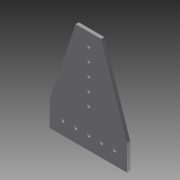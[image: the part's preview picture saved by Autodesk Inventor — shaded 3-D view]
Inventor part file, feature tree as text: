
AUTODESK INVENTOR PART (.ipt)
format: ipt  version: 2012 (Build 160160000, 160)  size: 92,160 bytes
history: native  units: in
note: dims shown in document units (in); Inventor stores cm internally (conversion verified against a paired STEP export)
features: extrude x1, sketch x1
ambient origin geometry x8: Origin, YZ Plane, XZ Plane, XY Plane, X Axis, Y Axis, Z Axis, Center Point
bodies: Solid1 (feature_tree)
feature tree (2):
  extrude  "Extrusion1"  Depth=3.0in
  sketch  "Sketch1"  dims[d0=1.0in d1=3.0in d2=4.0in d3=0.5in d4=0.5in d5=1.9685in d7=0.5in d8=0.3937in d10=1.0in d12=0.125in d13=0.5049in d14=0.5in d15=1.9685in d17=0.5in d18=0.3937in d20=1.0in d22=0.125in d23=0.0in]
